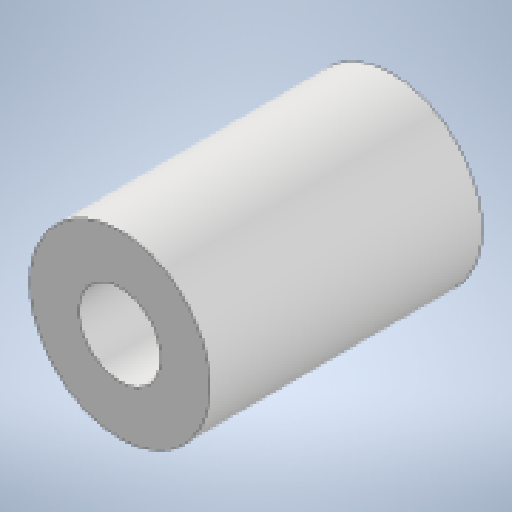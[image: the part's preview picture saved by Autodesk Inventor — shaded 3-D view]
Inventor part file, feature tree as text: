
AUTODESK INVENTOR PART (.ipt)
format: ipt  version: 2023 (Build 270158000, 158)  size: 137,216 bytes
history: native  units: in
note: dims shown in document units (in); Inventor stores cm internally (conversion verified against a paired STEP export)
features: sketch x1, plane x1, extrude x1
ambient origin geometry x8: Origin, YZ Plane, XZ Plane, XY Plane, X Axis, Y Axis, Z Axis, Center Point
bodies: Solid1 (feature_tree)
feature tree (3):
  sketch  "Sketch1"  dims[d0=0.17in d1=0.375in d2=1.0in d3=0.0in]
  plane  "Work Plane1"
  extrude  "Extrusion1"  Depth=0.375in
